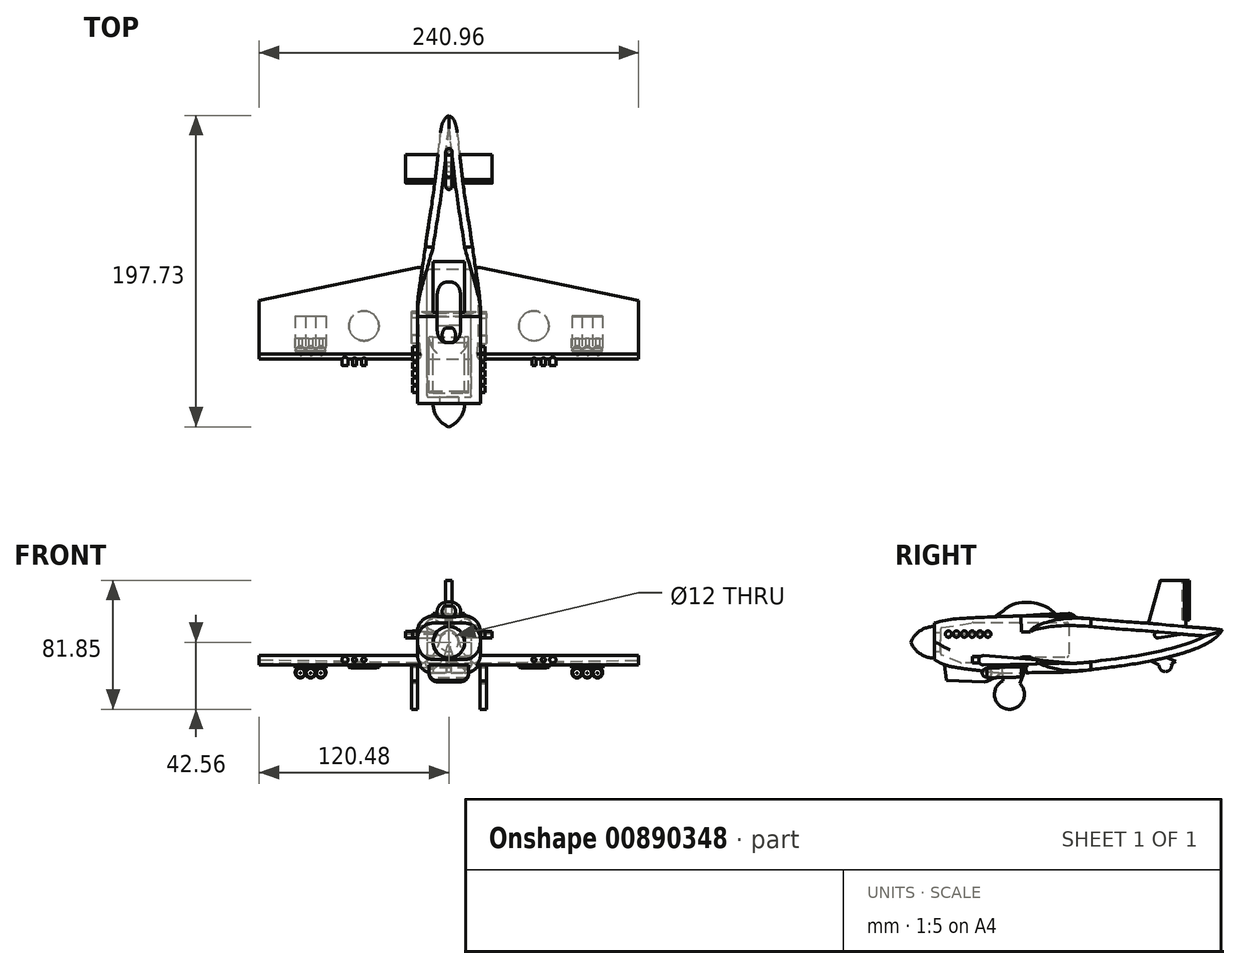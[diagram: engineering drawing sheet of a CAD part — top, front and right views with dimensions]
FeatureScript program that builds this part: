
annotation { "Feature Type Name" : "Feature", "Feature Type Description" : "" }
export const myFeature = defineFeature(function(context is Context, id is Id, definition is map)
    precondition{}
    {
        {
            var Q0;
            Q0=qCreatedBy(makeId("Right.planeOp"),FACE);
            var sketch = newSketch(context, id + "F0", { "sketchPlane" : qUnion([Q0])});
            skFitSpline(sketch, "E0", {"points": [v(0, 16.72) * mm, v(-14.24, 16.3) * mm, v(-32.71, 15.45) * mm, v(-55.08, 12.2) * mm], "startDerivative": vector(-47.41, -1.42) * mm, "endDerivative": vector(-61.1, -20.37) * mm});
            skFitSpline(sketch, "E1", {"points": [v(-55.08, -10.92) * mm, v(-48.5, -14.3) * mm, v(-31.02, -17.4) * mm, v(-12.83, -19.38) * mm, v(0, -19.52) * mm], "startDerivative": vector(34.18, -18.97) * mm, "endDerivative": vector(51.38, 0.82) * mm});
            skLineSegment(sketch, "E2", {"start": v(-55.08, 12.2) * mm, "end": v(-55.08, -10.92) * mm});
            skFitSpline(sketch, "E3", {"points": [v(0, -19.52) * mm, v(26.25, -19.04) * mm, v(50.38, -16.63) * mm, v(79.55, -12.4) * mm, v(113.94, -2.75) * mm, v(127.82, 7.9) * mm], "startDerivative": vector(117.96, 7.06) * mm, "endDerivative": vector(47.77, 80.25) * mm});
            skFitSpline(sketch, "E4", {"points": [v(0, 16.72) * mm, v(21.14, 16.46) * mm, v(44.97, 14.87) * mm, v(59.73, 13.57) * mm, v(82.02, 11.97) * mm, v(103.34, 10.02) * mm, v(127.82, 7.9) * mm], "startDerivative": vector(116.94, -1.03) * mm, "endDerivative": vector(53.67, -10.38) * mm});
            skLineSegment(sketch, "E5", {"start": v(-14.24, 16.3) * mm, "end": v(-12.51, 5.87) * mm});
            skLineSegment(sketch, "E6", {"start": v(-12.51, 5.87) * mm, "end": v(-15.87, -4.9) * mm});
            skLineSegment(sketch, "E7", {"start": v(-15.87, -4.9) * mm, "end": v(-23.28, -12.46) * mm});
            skLineSegment(sketch, "E8", {"start": v(-23.28, -12.46) * mm, "end": v(-31.02, -17.4) * mm});
            skLineSegment(sketch, "E9", {"start": v(-48.5, -14.3) * mm, "end": v(-47.42, -24.3) * mm});
            skLineSegment(sketch, "E10", {"start": v(-47.42, -24.3) * mm, "end": v(-22.16, -25.07) * mm});
            skLineSegment(sketch, "E11", {"start": v(-22.16, -25.07) * mm, "end": v(-16.61, -22.51) * mm});
            skLineSegment(sketch, "E12", {"start": v(-16.61, -22.51) * mm, "end": v(-12.83, -19.38) * mm});
            skSolve(sketch);
        }
        {
            var Q0;
            Q0=makeQuery(id+"F0.imprint","IMPRINT",FACE,{"disambiguationData":[TD([[makeQuery(id+"F0.imprint","IMPRINT",EDGE,{"derivedFrom":sQuery(id+"F0.wireOp",EDGE,"E0")}),1.0]])]});
            var Q1;
            {var subQ1=sQuery(id+"F0.wireOp",EDGE,"E3");Q1=makeQuery(id+"F0.imprint","IMPRINT",FACE,{"disambiguationData":[TD([[makeQuery(id+"F0.imprint","IMPRINT",EDGE,{"derivedFrom":subQ1}),1.0]])]});}
            extrude(context, id + "F1", {"entities" : qUnion([Q0, Q1]), "oppositeDirection" : true, "depth" : 20 * mm, "offsetDistance" : 25 * mm});
        }
        {
            var Q0;
            Q0=makeQuery(id+"F1.opExtrude","CAP_EDGE",EDGE,{"disambiguationData":[OSD([sQuery(id+"F0.wireOp",EDGE,"E4")])],"isStart":false});
            var Q1;
            Q1=makeQuery(id+"F1.opExtrude","CAP_EDGE",EDGE,{"disambiguationData":[OSD([sQuery(id+"F0.wireOp",EDGE,"E0")])],"isStart":false});
            var Q2;
            Q2=makeQuery(id+"F1.opExtrude","CAP_EDGE",EDGE,{"disambiguationData":[OSD([sQuery(id+"F0.wireOp",EDGE,"E3")])],"isStart":false});
            var Q3;
            Q3=makeQuery(id+"F1.opExtrude","CAP_EDGE",EDGE,{"disambiguationData":[OSD([sQuery(id+"F0.wireOp",EDGE,"E1")])],"isStart":false});
            fillet(context, id + "F2", {"entities" : qUnion([Q0, Q1, Q2, Q3]), "radius" : 10 * mm, "tangentPropagation" : true, "allowEdgeOverflow" : false});
        }
        {
            var Q0;
            Q0=qCreatedBy(makeId("Top.planeOp"),FACE);
            var sketch = newSketch(context, id + "F3", { "sketchPlane" : qUnion([Q0])});
            skFitSpline(sketch, "E13", {"points": [v(-3.69, 127.82) * mm, v(-8.55, 88.27) * mm, v(-13.04, 57.18) * mm, v(-17.19, 28.87) * mm, v(-20.17, 0) * mm], "startDerivative": vector(-19.1, -98.98) * mm, "endDerivative": vector(1.04, -111.2) * mm});
            skFitSpline(sketch, "E14.MirrorCS", {"points": [v(3.69, 127.82) * mm, v(8.55, 88.27) * mm, v(13.04, 57.18) * mm, v(17.19, 28.87) * mm, v(20.17, 0) * mm], "startDerivative": vector(19.1, -98.98) * mm, "endDerivative": vector(-1.04, -111.2) * mm});
            skLineSegment(sketch, "E15.bottom", {"start": v(-50.38, -63.43) * mm, "end": v(41.73, -63.43) * mm});
            skLineSegment(sketch, "E15.top", {"start": v(-50.38, 132.63) * mm, "end": v(41.73, 132.63) * mm});
            skLineSegment(sketch, "E15.left", {"start": v(-50.38, -63.43) * mm, "end": v(-50.38, 132.63) * mm});
            skLineSegment(sketch, "E15.right", {"start": v(41.73, -63.43) * mm, "end": v(41.73, 132.63) * mm});
            skLineSegment(sketch, "E16", {"start": v(-20.17, 0) * mm, "end": v(-50.38, 0) * mm});
            skLineSegment(sketch, "E17", {"start": v(20.17, 0) * mm, "end": v(41.73, 0) * mm});
            skLineSegment(sketch, "E18", {"start": v(-3.69, 127.82) * mm, "end": v(3.69, 127.82) * mm});
            skSolve(sketch);
        }
        {
            var Q0;
            Q0=makeQuery(id+"F3.imprint","IMPRINT",FACE,{"disambiguationData":[TD([[makeQuery(id+"F3.imprint","IMPRINT",EDGE,{"derivedFrom":sQuery(id+"F3.wireOp",EDGE,"E13")}),-1.0]])]});
            extrude(context, id + "F4", {"entities" : qUnion([Q0]), "operationType" : NewBodyOperationType.REMOVE, "oppositeDirection" : true, "depth" : 100 * mm, "offsetDistance" : 25 * mm, "symmetric" : true});
        }
        {
            var Q0;
            {var subQ0=sQuery(id+"F0.wireOp",EDGE,"E4");Q0=makeQuery(id+"F4.boolean.opBoolean","INTERSECT",EDGE,{"derivedFrom":[makeQuery(id+"F2.opFillet","BLEND_FACE",FACE,{"disambiguationData":[OSD([subQ0]),TDD([makeQuery(id+"F1.opExtrude","CAP_EDGE",EDGE,{"disambiguationData":[OSD([subQ0])],"isStart":true})])]}),makeQuery(id+"F4.opExtrude","SWEPT_FACE",FACE,{"disambiguationData":[OSD([sQuery(id+"F3.wireOp",EDGE,"E13")])]})]});}
            var Q1;
            {var subQ0=sQuery(id+"F0.wireOp",EDGE,"E4");Q1=makeQuery(id+"F4.boolean.opBoolean","INTERSECT",EDGE,{"derivedFrom":[makeQuery(id+"F2.opFillet","BLEND_FACE",FACE,{"disambiguationData":[OSD([subQ0]),TDD([makeQuery(id+"F1.opExtrude","CAP_EDGE",EDGE,{"disambiguationData":[OSD([subQ0])],"isStart":false})])]}),makeQuery(id+"F4.opExtrude","SWEPT_FACE",FACE,{"disambiguationData":[OSD([sQuery(id+"F3.wireOp",EDGE,"E14.MirrorCS")])]})]});}
            fillet(context, id + "F5", {"entities" : qUnion([Q0, Q1]), "radius" : 5 * mm, "tangentPropagation" : true, "allowEdgeOverflow" : false});
        }
        {
            var Q0;
            Q0=qCreatedBy(makeId("Right.planeOp"),FACE);
            var sketch = newSketch(context, id + "F6", { "sketchPlane" : qUnion([Q0])});
            skLineSegment(sketch, "E19", {"start": v(-16.45, 16.22) * mm, "end": v(-7.08, 23.21) * mm});
            skLineSegment(sketch, "E20", {"start": v(-7.08, 23.21) * mm, "end": v(-5.77, 16.56) * mm});
            skLineSegment(sketch, "E21", {"start": v(-5.77, 16.56) * mm, "end": v(-16.45, 16.22) * mm});
            skArc(sketch, "E22", {"start": v(21.96, 18.06) * mm, "mid": v(8.23, 25.06) * mm, "end": v(-7.08, 23.21) * mm});
            skLineSegment(sketch, "E23", {"start": v(-5.77, 16.56) * mm, "end": v(21.96, 18.06) * mm});
            skLineSegment(sketch, "E24", {"start": v(2.5, 16.7) * mm, "end": v(32.72, 18.34) * mm});
            skLineSegment(sketch, "E25", {"start": v(32.72, 18.34) * mm, "end": v(34.89, 15.69) * mm});
            skLineSegment(sketch, "E26", {"start": v(2.5, 16.7) * mm, "end": v(34.89, 15.69) * mm});
            skSolve(sketch);
        }
        {
            var Q0;
            Q0=makeQuery(id+"F6.imprint","IMPRINT",FACE,{"disambiguationData":[TD([[makeQuery(id+"F6.imprint","IMPRINT",EDGE,{"derivedFrom":sQuery(id+"F6.wireOp",EDGE,"E24")}),-1.0]])]});
            extrude(context, id + "F7", {"entities" : qUnion([Q0]), "operationType" : NewBodyOperationType.ADD, "oppositeDirection" : true, "depth" : 10 * mm, "offsetDistance" : 25 * mm});
        }
        {
            var Q0;
            Q0=makeQuery(id+"F6.imprint","IMPRINT",FACE,{"disambiguationData":[TD([[makeQuery(id+"F6.imprint","IMPRINT",EDGE,{"derivedFrom":sQuery(id+"F6.wireOp",EDGE,"E19")}),-1.0]])]});
            extrude(context, id + "F8", {"entities" : qUnion([Q0]), "operationType" : NewBodyOperationType.ADD, "oppositeDirection" : true, "depth" : 7.5 * mm, "offsetDistance" : 25 * mm});
        }
        {
            var Q0;
            Q0=makeQuery(id+"F6.imprint","IMPRINT",FACE,{"disambiguationData":[TD([[makeQuery(id+"F6.imprint","IMPRINT",EDGE,{"derivedFrom":sQuery(id+"F6.wireOp",EDGE,"E20")}),1.0]])]});
            extrude(context, id + "F9", {"entities" : qUnion([Q0]), "operationType" : NewBodyOperationType.ADD, "oppositeDirection" : true, "depth" : 7.5 * mm, "offsetDistance" : 25 * mm});
        }
        {
            var Q0;
            Q0=qCreatedBy(makeId("Right.planeOp"),FACE);
            var sketch = newSketch(context, id + "F10", { "sketchPlane" : qUnion([Q0])});
            skLineSegment(sketch, "E27", {"start": v(-51.08, 9.2) * mm, "end": v(-51.08, -7.92) * mm});
            skLineSegment(sketch, "E28", {"start": v(-51.08, 9.2) * mm, "end": v(-30.67, 12.45) * mm});
            skLineSegment(sketch, "E29", {"start": v(-30.67, 12.45) * mm, "end": v(-15.87, 12.45) * mm});
            skLineSegment(sketch, "E30", {"start": v(-15.87, 12.45) * mm, "end": v(-15.87, -13.07) * mm});
            skLineSegment(sketch, "E31", {"start": v(-15.87, -13.07) * mm, "end": v(-38.15, -13.07) * mm});
            skLineSegment(sketch, "E32", {"start": v(-38.15, -13.07) * mm, "end": v(-51.08, -7.92) * mm});
            skLineSegment(sketch, "E33.bottom", {"start": v(-15.87, 12.45) * mm, "end": v(30.26, 12.45) * mm});
            skLineSegment(sketch, "E33.top", {"start": v(-15.87, -9.27) * mm, "end": v(30.26, -9.27) * mm});
            skLineSegment(sketch, "E33.left", {"start": v(-15.87, 12.45) * mm, "end": v(-15.87, -9.27) * mm});
            skLineSegment(sketch, "E33.right", {"start": v(30.26, 12.45) * mm, "end": v(30.26, -9.27) * mm});
            skSolve(sketch);
        }
        {
            var Q0;
            Q0=makeQuery(id+"F10.imprint","IMPRINT",FACE,{"disambiguationData":[TD([[makeQuery(id+"F10.imprint","IMPRINT",EDGE,{"derivedFrom":sQuery(id+"F10.wireOp",EDGE,"E27")}),1.0]])]});
            var Q1;
            Q1=makeQuery(id+"F10.imprint","IMPRINT",FACE,{"disambiguationData":[TD([[makeQuery(id+"F10.imprint","IMPRINT",EDGE,{"derivedFrom":sQuery(id+"F10.wireOp",EDGE,"E33.bottom")}),-1.0]])]});
            extrude(context, id + "F11", {"entities" : qUnion([Q0, Q1]), "operationType" : NewBodyOperationType.REMOVE, "oppositeDirection" : true, "depth" : 14 * mm, "offsetDistance" : 25 * mm});
        }
        {
            var Q0;
            Q0=makeQuery(id+"F9.opExtrude","CAP_EDGE",EDGE,{"disambiguationData":[OSD([sQuery(id+"F6.wireOp",EDGE,"E22")])],"isStart":false});
            fillet(context, id + "F12", {"entities" : qUnion([Q0]), "radius" : 6 * mm, "tangentPropagation" : true, "allowEdgeOverflow" : false});
        }
        {
            var Q0;
            Q0=makeQuery(id+"F1.opExtrude","SWEPT_FACE",FACE,{"disambiguationData":[OSD([sQuery(id+"F0.wireOp",EDGE,"E2")])]});
            var sketch = newSketch(context, id + "F13", { "sketchPlane" : qUnion([Q0])});
            skCircle(sketch, "E34", {"center": v(0, 0) * mm, "radius": 6 * mm});
            skSolve(sketch);
        }
        {
            var Q0;
            {var subQ0=sQuery(id+"F13.wireOp",EDGE,"E34");var subQ1=makeQuery(id+"F1.opExtrude","CAP_EDGE",EDGE,{"disambiguationData":[OSD([sQuery(id+"F0.wireOp",EDGE,"E2")])],"isStart":true});var subQ2=makeQuery(id+"F13.imprint","INTERSECT",VERTEX,{"disambiguationData":[OD(0.0)],"derivedFrom":[subQ1,subQ0]});Q0=makeQuery(id+"F13.imprint","IMPRINT",FACE,{"disambiguationData":[TD([[makeQuery(id+"F13.imprint","IMPRINT",EDGE,{"disambiguationData":[TD([[subQ2,-1.0]])],"derivedFrom":subQ0}),1.0]])]});}
            extrude(context, id + "F14", {"entities" : qUnion([Q0]), "operationType" : NewBodyOperationType.REMOVE, "oppositeDirection" : true, "depth" : 25 * mm, "offsetDistance" : 25 * mm});
        }
        {
            var Q0;
            Q0=qCreatedBy(makeId("Right.planeOp"),FACE);
            var sketch = newSketch(context, id + "F15", { "sketchPlane" : qUnion([Q0])});
            skArc(sketch, "E35", {"start": v(-23.86, -8.47) * mm, "mid": v(-26.86, -11.47) * mm, "end": v(-23.86, -14.47) * mm});
            skLineSegment(sketch, "E36", {"start": v(-23.86, -8.47) * mm, "end": v(31.14, -13.1) * mm});
            skLineSegment(sketch, "E37", {"start": v(31.14, -13.1) * mm, "end": v(-23.86, -14.47) * mm});
            skArc(sketch, "E38", {"start": v(87.08, 6.72) * mm, "mid": v(84.75, 4.75) * mm, "end": v(87.08, 2.78) * mm});
            skLineSegment(sketch, "E39", {"start": v(87.08, 6.72) * mm, "end": v(103.03, 5.17) * mm});
            skLineSegment(sketch, "E40", {"start": v(103.03, 5.17) * mm, "end": v(87.08, 2.78) * mm});
            skSolve(sketch);
        }
        {
            var Q0;
            Q0=makeQuery(id+"F15.imprint","IMPRINT",FACE,{"disambiguationData":[TD([[makeQuery(id+"F15.imprint","IMPRINT",EDGE,{"derivedFrom":sQuery(id+"F15.wireOp",EDGE,"E35")}),1.0]])]});
            extrude(context, id + "F16", {"entities" : qUnion([Q0]), "operationType" : NewBodyOperationType.ADD, "oppositeDirection" : true, "depth" : 25 * mm, "offsetDistance" : 25 * mm});
        }
        {
            var Q0;
            Q0=makeQuery(id+"F16.opExtrude","CAP_FACE",FACE,{"disambiguationData":[OSD([sQuery(id+"F15.wireOp",EDGE,"E35"),sQuery(id+"F15.wireOp",EDGE,"E36"),sQuery(id+"F15.wireOp",EDGE,"E37")])],"isStart":false});
            extrude(context, id + "F17", {"entities" : qUnion([Q0]), "operationType" : NewBodyOperationType.ADD, "depth" : 100 * mm, "offsetDistance" : 25 * mm});
        }
        {
            var Q0;
            {var subQ0=sQuery(id+"F15.wireOp",EDGE,"E36");var subQ4=sQuery(id+"F0.wireOp",EDGE,"E1");Q0=makeQuery(id+"F17.boolean.opBoolean","MERGE",FACE,{"derivedFrom":[makeQuery(id+"F16.boolean.opBoolean","SPLIT",FACE,{"disambiguationData":[TD([makeQuery(id+"F2.opFillet","BLEND_FACE",FACE,{"disambiguationData":[OSD([subQ4]),TDD([makeQuery(id+"F1.opExtrude","CAP_EDGE",EDGE,{"disambiguationData":[OSD([subQ4])],"isStart":false})])]})])],"derivedFrom":makeQuery(id+"F16.opExtrude","SWEPT_FACE",FACE,{"disambiguationData":[OSD([subQ0])]})}),makeQuery(id+"F17.opExtrude","SWEPT_FACE",FACE,{"disambiguationData":[OSD([subQ0])]})]});}
            var sketch = newSketch(context, id + "F18", { "sketchPlane" : qUnion([Q0])});
            skLineSegment(sketch, "E41", {"start": v(19.74, 32.12) * mm, "end": v(120.48, 11.31) * mm});
            skLineSegment(sketch, "E42", {"start": v(120.48, 11.31) * mm, "end": v(120.48, -23.07) * mm});
            skLineSegment(sketch, "E43", {"start": v(120.48, -23.07) * mm, "end": v(-125, -23.07) * mm});
            skLineSegment(sketch, "E44", {"start": v(19.74, 32.12) * mm, "end": v(22.37, 44.82) * mm});
            skLineSegment(sketch, "E45", {"start": v(22.37, 44.82) * mm, "end": v(134.96, 44.82) * mm});
            skLineSegment(sketch, "E46", {"start": v(134.96, 44.82) * mm, "end": v(134.96, -23.07) * mm});
            skLineSegment(sketch, "E47", {"start": v(134.96, -23.07) * mm, "end": v(120.48, -23.07) * mm});
            skLineSegment(sketch, "E48", {"start": v(120.48, -23.07) * mm, "end": v(120.48, -30.04) * mm});
            skLineSegment(sketch, "E49", {"start": v(120.48, -30.04) * mm, "end": v(134.77, -30) * mm});
            skLineSegment(sketch, "E50", {"start": v(134.77, -30) * mm, "end": v(134.96, -23.07) * mm});
            skLineSegment(sketch, "E51.MirrorCS", {"start": v(-22.37, 44.82) * mm, "end": v(-134.96, 44.82) * mm});
            skLineSegment(sketch, "E52.MirrorCS", {"start": v(-19.74, 32.12) * mm, "end": v(-22.37, 44.82) * mm});
            skLineSegment(sketch, "E53.MirrorCS", {"start": v(-19.74, 32.12) * mm, "end": v(-120.48, 11.31) * mm});
            skLineSegment(sketch, "E54.MirrorCS", {"start": v(-134.96, 44.82) * mm, "end": v(-134.96, -23.07) * mm});
            skLineSegment(sketch, "E55.MirrorCS", {"start": v(-120.48, -30.04) * mm, "end": v(-134.77, -30) * mm});
            skLineSegment(sketch, "E56.MirrorCS", {"start": v(-120.48, -23.07) * mm, "end": v(-120.48, -30.04) * mm});
            skLineSegment(sketch, "E57.MirrorCS", {"start": v(-134.77, -30) * mm, "end": v(-134.96, -23.07) * mm});
            skLineSegment(sketch, "E58.MirrorCS", {"start": v(-120.48, 11.31) * mm, "end": v(-120.48, -23.07) * mm});
            skSolve(sketch);
        }
        {
            var Q0;
            Q0=makeQuery(id+"F18.imprint","IMPRINT",FACE,{"disambiguationData":[TD([[makeQuery(id+"F18.imprint","IMPRINT",EDGE,{"derivedFrom":sQuery(id+"F18.wireOp",EDGE,"E51.MirrorCS")}),1.0]])]});
            var Q1;
            {var subQ1=sQuery(id+"F18.wireOp",EDGE,"E53.MirrorCS");Q1=makeQuery(id+"F18.imprint","IMPRINT",FACE,{"disambiguationData":[TD([[makeQuery(id+"F18.imprint","IMPRINT",EDGE,{"derivedFrom":subQ1}),-1.0]])]});}
            extrude(context, id + "F19", {"entities" : qUnion([Q0, Q1]), "operationType" : NewBodyOperationType.REMOVE, "oppositeDirection" : true, "depth" : 25 * mm, "offsetDistance" : 25 * mm});
        }
        {
            var Q0;
            Q0=qCreatedBy(makeId("Right.planeOp"),FACE);
            var sketch = newSketch(context, id + "F20", { "sketchPlane" : qUnion([Q0])});
            skLineSegment(sketch, "E59", {"start": v(80.82, 12.07) * mm, "end": v(88.57, 39.3) * mm});
            skLineSegment(sketch, "E60", {"start": v(88.57, 39.3) * mm, "end": v(104.75, 39.3) * mm});
            skLineSegment(sketch, "E61", {"start": v(104.75, 39.3) * mm, "end": v(104.75, 9.9) * mm});
            skLineSegment(sketch, "E62", {"start": v(104.75, 9.9) * mm, "end": v(80.82, 12.07) * mm});
            skLineSegment(sketch, "E63.bottom", {"start": v(106.73, 39.3) * mm, "end": v(118.95, 39.3) * mm});
            skLineSegment(sketch, "E63.top", {"start": v(106.73, 11.19) * mm, "end": v(118.95, 11.19) * mm});
            skLineSegment(sketch, "E63.left", {"start": v(106.73, 39.3) * mm, "end": v(106.73, 11.19) * mm});
            skLineSegment(sketch, "E63.right", {"start": v(118.95, 39.3) * mm, "end": v(118.95, 11.19) * mm});
            skLineSegment(sketch, "E64.bottom", {"start": v(104.75, 34.79) * mm, "end": v(106.73, 34.79) * mm});
            skLineSegment(sketch, "E64.top", {"start": v(104.75, 31.59) * mm, "end": v(106.73, 31.59) * mm});
            skLineSegment(sketch, "E64.left", {"start": v(104.75, 34.79) * mm, "end": v(104.75, 31.59) * mm});
            skLineSegment(sketch, "E64.right", {"start": v(106.73, 34.79) * mm, "end": v(106.73, 31.59) * mm});
            skLineSegment(sketch, "E65.bottom", {"start": v(104.75, 22.93) * mm, "end": v(106.73, 22.93) * mm});
            skLineSegment(sketch, "E65.top", {"start": v(104.75, 18.78) * mm, "end": v(106.73, 18.78) * mm});
            skLineSegment(sketch, "E65.left", {"start": v(104.75, 22.93) * mm, "end": v(104.75, 18.78) * mm});
            skLineSegment(sketch, "E65.right", {"start": v(106.73, 22.93) * mm, "end": v(106.73, 18.78) * mm});
            skLineSegment(sketch, "E66", {"start": v(80.82, 12.07) * mm, "end": v(80.49, 8.43) * mm});
            skLineSegment(sketch, "E67", {"start": v(80.49, 8.43) * mm, "end": v(104.27, 6.28) * mm});
            skLineSegment(sketch, "E68", {"start": v(104.27, 6.28) * mm, "end": v(104.75, 9.9) * mm});
            skSolve(sketch);
        }
        {
            var Q0;
            Q0=makeQuery(id+"F20.imprint","IMPRINT",FACE,{"disambiguationData":[TD([[makeQuery(id+"F20.imprint","IMPRINT",EDGE,{"derivedFrom":sQuery(id+"F20.wireOp",EDGE,"E59")}),-1.0]])]});
            var Q1;
            Q1=makeQuery(id+"F20.imprint","IMPRINT",FACE,{"disambiguationData":[TD([[makeQuery(id+"F20.imprint","IMPRINT",EDGE,{"derivedFrom":sQuery(id+"F20.wireOp",EDGE,"E62")}),1.0]])]});
            extrude(context, id + "F21", {"entities" : qUnion([Q0, Q1]), "operationType" : NewBodyOperationType.ADD, "oppositeDirection" : true, "depth" : 2 * mm, "offsetDistance" : 25 * mm});
        }
        {
            var Q0;
            Q0=makeQuery(id+"F21.opExtrude","SWEPT_FACE",FACE,{"disambiguationData":[OSD([sQuery(id+"F20.wireOp",EDGE,"E60")])]});
            var sketch = newSketch(context, id + "F22", { "sketchPlane" : qUnion([Q0])});
            skArc(sketch, "E69", {"start": v(0, 102.75) * mm, "mid": v(-2, 104.75) * mm, "end": v(0, 106.75) * mm});
            skArc(sketch, "E70", {"start": v(0, 102.55) * mm, "mid": v(-1.56, 103.19) * mm, "end": v(-2.2, 104.75) * mm});
            skLineSegment(sketch, "E71", {"start": v(-2, 104.75) * mm, "end": v(0, 119.75) * mm});
            skLineSegment(sketch, "E72", {"start": v(0, 119.75) * mm, "end": v(0, 104.75) * mm});
            skLineSegment(sketch, "E73", {"start": v(0, 102.55) * mm, "end": v(0, 102.75) * mm});
            skLineSegment(sketch, "E74", {"start": v(0, 102.75) * mm, "end": v(0, 104.75) * mm});
            skLineSegment(sketch, "E75", {"start": v(0, 104.75) * mm, "end": v(-2, 104.75) * mm});
            skSolve(sketch);
        }
        {
            var Q0;
            {var subQ2=sQuery(id+"F22.wireOp",EDGE,"E74");Q0=makeQuery(id+"F22.imprint","IMPRINT",FACE,{"disambiguationData":[TD([[makeQuery(id+"F22.imprint","IMPRINT",EDGE,{"derivedFrom":subQ2}),1.0]])]});}
            var Q1;
            {var subQ5=sQuery(id+"F22.wireOp",EDGE,"E75");Q1=makeQuery(id+"F22.imprint","IMPRINT",FACE,{"disambiguationData":[TD([[makeQuery(id+"F22.imprint","IMPRINT",EDGE,{"derivedFrom":subQ5}),1.0]])]});}
            var Q2;
            {var subQ0=sQuery(id+"F22.wireOp",EDGE,"E72");var subQ1=sQuery(id+"F22.wireOp",EDGE,"E69");var subQ2=makeQuery(id+"F22.imprint","INTERSECT",VERTEX,{"derivedFrom":[subQ1,subQ0]});Q2=makeQuery(id+"F22.imprint","IMPRINT",FACE,{"disambiguationData":[TD([[makeQuery(id+"F22.imprint","IMPRINT",EDGE,{"disambiguationData":[TD([[subQ2,1.0]])],"derivedFrom":subQ1}),1.0]])]});}
            extrude(context, id + "F23", {"entities" : qUnion([Q0, Q1, Q2]), "operationType" : NewBodyOperationType.ADD, "oppositeDirection" : true, "depth" : 25 * mm, "offsetDistance" : 25 * mm});
        }
        {
            var Q0;
            {var subQ4=sQuery(id+"F22.wireOp",EDGE,"E73");Q0=makeQuery(id+"F22.imprint","IMPRINT",FACE,{"disambiguationData":[TD([[makeQuery(id+"F22.imprint","IMPRINT",EDGE,{"derivedFrom":subQ4}),1.0]])]});}
            extrude(context, id + "F24", {"entities" : qUnion([Q0]), "operationType" : NewBodyOperationType.REMOVE, "oppositeDirection" : true, "depth" : 25 * mm, "offsetDistance" : 25 * mm});
        }
        {
            var Q0;
            Q0=makeQuery(id+"F1.opExtrude","SWEPT_FACE",FACE,{"disambiguationData":[OSD([sQuery(id+"F0.wireOp",EDGE,"E2")])]});
            var sketch = newSketch(context, id + "F25", { "sketchPlane" : qUnion([Q0])});
            skCircle(sketch, "E76", {"center": v(0, 0) * mm, "radius": 10 * mm});
            skSolve(sketch);
        }
        {
            var Q0;
            Q0=qCreatedBy(makeId("Right.planeOp"),FACE);
            var sketch = newSketch(context, id + "F26", { "sketchPlane" : qUnion([Q0])});
            skArc(sketch, "E77", {"start": v(-55.08, 10) * mm, "mid": v(-64.1, 7.3) * mm, "end": v(-70.03, 0) * mm});
            skArc(sketch, "E78.MirrorCS", {"start": v(-55.08, -10) * mm, "mid": v(-64.1, -7.3) * mm, "end": v(-70.03, 0) * mm});
            skLineSegment(sketch, "E79", {"start": v(-70.03, 0) * mm, "end": v(-55.08, 0) * mm});
            skLineSegment(sketch, "E80", {"start": v(-55.08, 10) * mm, "end": v(-55.08, -10) * mm});
            skSolve(sketch);
        }
        {
            var Q0;
            {var subQ0=sQuery(id+"F26.wireOp",EDGE,"E77");Q0=makeQuery(id+"F26.imprint","IMPRINT",FACE,{"disambiguationData":[TD([[makeQuery(id+"F26.imprint","IMPRINT",EDGE,{"derivedFrom":subQ0}),1.0]])]});}
            var Q1;
            Q1=sQuery(id+"F26.wireOp",EDGE,"E79");
            revolve(context, id + "F27", {"surfaceOperationType" : NewSurfaceOperationType.NEW, "entities" : qUnion([Q0]), "axis" : qUnion([Q1]), "revolveType" : RevolveType.FULL});
        }
        {
            var Q0;
            Q0=makeQuery(id+"F1.opExtrude","CAP_FACE",FACE,{"disambiguationData":[OSD([sQuery(id+"F0.wireOp",EDGE,"E0"),sQuery(id+"F0.wireOp",EDGE,"E1"),sQuery(id+"F0.wireOp",EDGE,"E2"),sQuery(id+"F0.wireOp",EDGE,"E3"),sQuery(id+"F0.wireOp",EDGE,"E4")])],"isStart":false});
            var sketch = newSketch(context, id + "F28", { "sketchPlane" : qUnion([Q0])});
            skCircle(sketch, "E81", {"center": v(26.08, 5.2) * mm, "radius": 2 * mm});
            skCircle(sketch, "E82", {"center": v(31.08, 5.2) * mm, "radius": 2 * mm});
            skCircle(sketch, "E83", {"center": v(36.08, 5.2) * mm, "radius": 2 * mm});
            skCircle(sketch, "E84", {"center": v(41.08, 5.2) * mm, "radius": 2 * mm});
            skCircle(sketch, "E85", {"center": v(46.08, 5.2) * mm, "radius": 2 * mm});
            skCircle(sketch, "E86", {"center": v(21.08, 5.2) * mm, "radius": 2 * mm});
            skSolve(sketch);
        }
        {
            var Q0;
            {var subQ0=sQuery(id+"F28.wireOp",EDGE,"E86");var subQ1=sQuery(id+"F0.wireOp",EDGE,"E0");var subQ2=makeQuery(id+"F2.opFillet","BLEND_EDGE",EDGE,{"blendedFrom":[makeQuery(id+"F1.opExtrude","CAP_EDGE",EDGE,{"disambiguationData":[OSD([subQ1])],"isStart":false}),makeQuery(id+"F1.opExtrude","CAP_FACE",FACE,{"disambiguationData":[OSD([subQ1,sQuery(id+"F0.wireOp",EDGE,"E1"),sQuery(id+"F0.wireOp",EDGE,"E2"),sQuery(id+"F0.wireOp",EDGE,"E3"),sQuery(id+"F0.wireOp",EDGE,"E4")])],"isStart":false})],"blendedInto":[makeQuery(id+"F1.opExtrude","CAP_FACE",FACE,{"disambiguationData":[OSD([subQ1,sQuery(id+"F0.wireOp",EDGE,"E1"),sQuery(id+"F0.wireOp",EDGE,"E2"),sQuery(id+"F0.wireOp",EDGE,"E3"),sQuery(id+"F0.wireOp",EDGE,"E4")])],"isStart":false})]});var subQ3=makeQuery(id+"F28.imprint","INTERSECT",VERTEX,{"disambiguationData":[OD(0.0)],"derivedFrom":[subQ2,subQ0]});Q0=makeQuery(id+"F28.imprint","IMPRINT",FACE,{"disambiguationData":[TD([[makeQuery(id+"F28.imprint","IMPRINT",EDGE,{"disambiguationData":[TD([[subQ3,1.0]])],"derivedFrom":subQ0}),1.0]])]});}
            var Q1;
            {var subQ0=sQuery(id+"F28.wireOp",EDGE,"E86");var subQ1=sQuery(id+"F0.wireOp",EDGE,"E0");var subQ2=makeQuery(id+"F2.opFillet","BLEND_EDGE",EDGE,{"blendedFrom":[makeQuery(id+"F1.opExtrude","CAP_EDGE",EDGE,{"disambiguationData":[OSD([subQ1])],"isStart":false}),makeQuery(id+"F1.opExtrude","CAP_FACE",FACE,{"disambiguationData":[OSD([subQ1,sQuery(id+"F0.wireOp",EDGE,"E1"),sQuery(id+"F0.wireOp",EDGE,"E2"),sQuery(id+"F0.wireOp",EDGE,"E3"),sQuery(id+"F0.wireOp",EDGE,"E4")])],"isStart":false})],"blendedInto":[makeQuery(id+"F1.opExtrude","CAP_FACE",FACE,{"disambiguationData":[OSD([subQ1,sQuery(id+"F0.wireOp",EDGE,"E1"),sQuery(id+"F0.wireOp",EDGE,"E2"),sQuery(id+"F0.wireOp",EDGE,"E3"),sQuery(id+"F0.wireOp",EDGE,"E4")])],"isStart":false})]});var subQ3=makeQuery(id+"F28.imprint","INTERSECT",VERTEX,{"disambiguationData":[OD(0.0)],"derivedFrom":[subQ2,subQ0]});Q1=makeQuery(id+"F28.imprint","IMPRINT",FACE,{"disambiguationData":[TD([[makeQuery(id+"F28.imprint","IMPRINT",EDGE,{"disambiguationData":[TD([[subQ3,-1.0]])],"derivedFrom":subQ0}),1.0]])]});}
            var Q2;
            {var subQ0=sQuery(id+"F28.wireOp",EDGE,"E81");var subQ1=sQuery(id+"F0.wireOp",EDGE,"E0");var subQ2=makeQuery(id+"F2.opFillet","BLEND_EDGE",EDGE,{"blendedFrom":[makeQuery(id+"F1.opExtrude","CAP_EDGE",EDGE,{"disambiguationData":[OSD([subQ1])],"isStart":false}),makeQuery(id+"F1.opExtrude","CAP_FACE",FACE,{"disambiguationData":[OSD([subQ1,sQuery(id+"F0.wireOp",EDGE,"E1"),sQuery(id+"F0.wireOp",EDGE,"E2"),sQuery(id+"F0.wireOp",EDGE,"E3"),sQuery(id+"F0.wireOp",EDGE,"E4")])],"isStart":false})],"blendedInto":[makeQuery(id+"F1.opExtrude","CAP_FACE",FACE,{"disambiguationData":[OSD([subQ1,sQuery(id+"F0.wireOp",EDGE,"E1"),sQuery(id+"F0.wireOp",EDGE,"E2"),sQuery(id+"F0.wireOp",EDGE,"E3"),sQuery(id+"F0.wireOp",EDGE,"E4")])],"isStart":false})]});var subQ3=makeQuery(id+"F28.imprint","INTERSECT",VERTEX,{"disambiguationData":[OD(0.0)],"derivedFrom":[subQ2,subQ0]});Q2=makeQuery(id+"F28.imprint","IMPRINT",FACE,{"disambiguationData":[TD([[makeQuery(id+"F28.imprint","IMPRINT",EDGE,{"disambiguationData":[TD([[subQ3,-1.0]])],"derivedFrom":subQ0}),1.0]])]});}
            var Q3;
            {var subQ0=sQuery(id+"F28.wireOp",EDGE,"E81");var subQ1=sQuery(id+"F0.wireOp",EDGE,"E0");var subQ2=makeQuery(id+"F2.opFillet","BLEND_EDGE",EDGE,{"blendedFrom":[makeQuery(id+"F1.opExtrude","CAP_EDGE",EDGE,{"disambiguationData":[OSD([subQ1])],"isStart":false}),makeQuery(id+"F1.opExtrude","CAP_FACE",FACE,{"disambiguationData":[OSD([subQ1,sQuery(id+"F0.wireOp",EDGE,"E1"),sQuery(id+"F0.wireOp",EDGE,"E2"),sQuery(id+"F0.wireOp",EDGE,"E3"),sQuery(id+"F0.wireOp",EDGE,"E4")])],"isStart":false})],"blendedInto":[makeQuery(id+"F1.opExtrude","CAP_FACE",FACE,{"disambiguationData":[OSD([subQ1,sQuery(id+"F0.wireOp",EDGE,"E1"),sQuery(id+"F0.wireOp",EDGE,"E2"),sQuery(id+"F0.wireOp",EDGE,"E3"),sQuery(id+"F0.wireOp",EDGE,"E4")])],"isStart":false})]});var subQ3=makeQuery(id+"F28.imprint","INTERSECT",VERTEX,{"disambiguationData":[OD(0.0)],"derivedFrom":[subQ2,subQ0]});Q3=makeQuery(id+"F28.imprint","IMPRINT",FACE,{"disambiguationData":[TD([[makeQuery(id+"F28.imprint","IMPRINT",EDGE,{"disambiguationData":[TD([[subQ3,1.0]])],"derivedFrom":subQ0}),1.0]])]});}
            var Q4;
            {var subQ0=sQuery(id+"F28.wireOp",EDGE,"E82");var subQ1=sQuery(id+"F0.wireOp",EDGE,"E0");var subQ2=makeQuery(id+"F2.opFillet","BLEND_EDGE",EDGE,{"blendedFrom":[makeQuery(id+"F1.opExtrude","CAP_EDGE",EDGE,{"disambiguationData":[OSD([subQ1])],"isStart":false}),makeQuery(id+"F1.opExtrude","CAP_FACE",FACE,{"disambiguationData":[OSD([subQ1,sQuery(id+"F0.wireOp",EDGE,"E1"),sQuery(id+"F0.wireOp",EDGE,"E2"),sQuery(id+"F0.wireOp",EDGE,"E3"),sQuery(id+"F0.wireOp",EDGE,"E4")])],"isStart":false})],"blendedInto":[makeQuery(id+"F1.opExtrude","CAP_FACE",FACE,{"disambiguationData":[OSD([subQ1,sQuery(id+"F0.wireOp",EDGE,"E1"),sQuery(id+"F0.wireOp",EDGE,"E2"),sQuery(id+"F0.wireOp",EDGE,"E3"),sQuery(id+"F0.wireOp",EDGE,"E4")])],"isStart":false})]});var subQ3=makeQuery(id+"F28.imprint","INTERSECT",VERTEX,{"disambiguationData":[OD(0.0)],"derivedFrom":[subQ2,subQ0]});Q4=makeQuery(id+"F28.imprint","IMPRINT",FACE,{"disambiguationData":[TD([[makeQuery(id+"F28.imprint","IMPRINT",EDGE,{"disambiguationData":[TD([[subQ3,-1.0]])],"derivedFrom":subQ0}),1.0]])]});}
            var Q5;
            {var subQ0=sQuery(id+"F28.wireOp",EDGE,"E83");var subQ1=sQuery(id+"F0.wireOp",EDGE,"E0");var subQ2=makeQuery(id+"F2.opFillet","BLEND_EDGE",EDGE,{"blendedFrom":[makeQuery(id+"F1.opExtrude","CAP_EDGE",EDGE,{"disambiguationData":[OSD([subQ1])],"isStart":false}),makeQuery(id+"F1.opExtrude","CAP_FACE",FACE,{"disambiguationData":[OSD([subQ1,sQuery(id+"F0.wireOp",EDGE,"E1"),sQuery(id+"F0.wireOp",EDGE,"E2"),sQuery(id+"F0.wireOp",EDGE,"E3"),sQuery(id+"F0.wireOp",EDGE,"E4")])],"isStart":false})],"blendedInto":[makeQuery(id+"F1.opExtrude","CAP_FACE",FACE,{"disambiguationData":[OSD([subQ1,sQuery(id+"F0.wireOp",EDGE,"E1"),sQuery(id+"F0.wireOp",EDGE,"E2"),sQuery(id+"F0.wireOp",EDGE,"E3"),sQuery(id+"F0.wireOp",EDGE,"E4")])],"isStart":false})]});var subQ3=makeQuery(id+"F28.imprint","INTERSECT",VERTEX,{"disambiguationData":[OD(0.0)],"derivedFrom":[subQ2,subQ0]});Q5=makeQuery(id+"F28.imprint","IMPRINT",FACE,{"disambiguationData":[TD([[makeQuery(id+"F28.imprint","IMPRINT",EDGE,{"disambiguationData":[TD([[subQ3,1.0]])],"derivedFrom":subQ0}),1.0]])]});}
            var Q6;
            {var subQ0=sQuery(id+"F28.wireOp",EDGE,"E84");var subQ1=sQuery(id+"F0.wireOp",EDGE,"E0");var subQ2=makeQuery(id+"F2.opFillet","BLEND_EDGE",EDGE,{"blendedFrom":[makeQuery(id+"F1.opExtrude","CAP_EDGE",EDGE,{"disambiguationData":[OSD([subQ1])],"isStart":false}),makeQuery(id+"F1.opExtrude","CAP_FACE",FACE,{"disambiguationData":[OSD([subQ1,sQuery(id+"F0.wireOp",EDGE,"E1"),sQuery(id+"F0.wireOp",EDGE,"E2"),sQuery(id+"F0.wireOp",EDGE,"E3"),sQuery(id+"F0.wireOp",EDGE,"E4")])],"isStart":false})],"blendedInto":[makeQuery(id+"F1.opExtrude","CAP_FACE",FACE,{"disambiguationData":[OSD([subQ1,sQuery(id+"F0.wireOp",EDGE,"E1"),sQuery(id+"F0.wireOp",EDGE,"E2"),sQuery(id+"F0.wireOp",EDGE,"E3"),sQuery(id+"F0.wireOp",EDGE,"E4")])],"isStart":false})]});var subQ3=makeQuery(id+"F28.imprint","INTERSECT",VERTEX,{"disambiguationData":[OD(0.0)],"derivedFrom":[subQ2,subQ0]});Q6=makeQuery(id+"F28.imprint","IMPRINT",FACE,{"disambiguationData":[TD([[makeQuery(id+"F28.imprint","IMPRINT",EDGE,{"disambiguationData":[TD([[subQ3,1.0]])],"derivedFrom":subQ0}),1.0]])]});}
            var Q7;
            {var subQ0=sQuery(id+"F28.wireOp",EDGE,"E85");var subQ1=sQuery(id+"F0.wireOp",EDGE,"E0");var subQ2=makeQuery(id+"F2.opFillet","BLEND_EDGE",EDGE,{"blendedFrom":[makeQuery(id+"F1.opExtrude","CAP_EDGE",EDGE,{"disambiguationData":[OSD([subQ1])],"isStart":false}),makeQuery(id+"F1.opExtrude","CAP_FACE",FACE,{"disambiguationData":[OSD([subQ1,sQuery(id+"F0.wireOp",EDGE,"E1"),sQuery(id+"F0.wireOp",EDGE,"E2"),sQuery(id+"F0.wireOp",EDGE,"E3"),sQuery(id+"F0.wireOp",EDGE,"E4")])],"isStart":false})],"blendedInto":[makeQuery(id+"F1.opExtrude","CAP_FACE",FACE,{"disambiguationData":[OSD([subQ1,sQuery(id+"F0.wireOp",EDGE,"E1"),sQuery(id+"F0.wireOp",EDGE,"E2"),sQuery(id+"F0.wireOp",EDGE,"E3"),sQuery(id+"F0.wireOp",EDGE,"E4")])],"isStart":false})]});var subQ3=makeQuery(id+"F28.imprint","INTERSECT",VERTEX,{"disambiguationData":[OD(0.0)],"derivedFrom":[subQ2,subQ0]});Q7=makeQuery(id+"F28.imprint","IMPRINT",FACE,{"disambiguationData":[TD([[makeQuery(id+"F28.imprint","IMPRINT",EDGE,{"disambiguationData":[TD([[subQ3,1.0]])],"derivedFrom":subQ0}),1.0]])]});}
            var Q8;
            {var subQ0=sQuery(id+"F28.wireOp",EDGE,"E85");var subQ1=sQuery(id+"F0.wireOp",EDGE,"E0");var subQ2=makeQuery(id+"F2.opFillet","BLEND_EDGE",EDGE,{"blendedFrom":[makeQuery(id+"F1.opExtrude","CAP_EDGE",EDGE,{"disambiguationData":[OSD([subQ1])],"isStart":false}),makeQuery(id+"F1.opExtrude","CAP_FACE",FACE,{"disambiguationData":[OSD([subQ1,sQuery(id+"F0.wireOp",EDGE,"E1"),sQuery(id+"F0.wireOp",EDGE,"E2"),sQuery(id+"F0.wireOp",EDGE,"E3"),sQuery(id+"F0.wireOp",EDGE,"E4")])],"isStart":false})],"blendedInto":[makeQuery(id+"F1.opExtrude","CAP_FACE",FACE,{"disambiguationData":[OSD([subQ1,sQuery(id+"F0.wireOp",EDGE,"E1"),sQuery(id+"F0.wireOp",EDGE,"E2"),sQuery(id+"F0.wireOp",EDGE,"E3"),sQuery(id+"F0.wireOp",EDGE,"E4")])],"isStart":false})]});var subQ3=makeQuery(id+"F28.imprint","INTERSECT",VERTEX,{"disambiguationData":[OD(0.0)],"derivedFrom":[subQ2,subQ0]});Q8=makeQuery(id+"F28.imprint","IMPRINT",FACE,{"disambiguationData":[TD([[makeQuery(id+"F28.imprint","IMPRINT",EDGE,{"disambiguationData":[TD([[subQ3,-1.0]])],"derivedFrom":subQ0}),1.0]])]});}
            var Q9;
            {var subQ0=sQuery(id+"F28.wireOp",EDGE,"E84");var subQ1=sQuery(id+"F0.wireOp",EDGE,"E0");var subQ2=makeQuery(id+"F2.opFillet","BLEND_EDGE",EDGE,{"blendedFrom":[makeQuery(id+"F1.opExtrude","CAP_EDGE",EDGE,{"disambiguationData":[OSD([subQ1])],"isStart":false}),makeQuery(id+"F1.opExtrude","CAP_FACE",FACE,{"disambiguationData":[OSD([subQ1,sQuery(id+"F0.wireOp",EDGE,"E1"),sQuery(id+"F0.wireOp",EDGE,"E2"),sQuery(id+"F0.wireOp",EDGE,"E3"),sQuery(id+"F0.wireOp",EDGE,"E4")])],"isStart":false})],"blendedInto":[makeQuery(id+"F1.opExtrude","CAP_FACE",FACE,{"disambiguationData":[OSD([subQ1,sQuery(id+"F0.wireOp",EDGE,"E1"),sQuery(id+"F0.wireOp",EDGE,"E2"),sQuery(id+"F0.wireOp",EDGE,"E3"),sQuery(id+"F0.wireOp",EDGE,"E4")])],"isStart":false})]});var subQ3=makeQuery(id+"F28.imprint","INTERSECT",VERTEX,{"disambiguationData":[OD(0.0)],"derivedFrom":[subQ2,subQ0]});Q9=makeQuery(id+"F28.imprint","IMPRINT",FACE,{"disambiguationData":[TD([[makeQuery(id+"F28.imprint","IMPRINT",EDGE,{"disambiguationData":[TD([[subQ3,-1.0]])],"derivedFrom":subQ0}),1.0]])]});}
            var Q10;
            {var subQ0=sQuery(id+"F28.wireOp",EDGE,"E83");var subQ1=sQuery(id+"F0.wireOp",EDGE,"E0");var subQ2=makeQuery(id+"F2.opFillet","BLEND_EDGE",EDGE,{"blendedFrom":[makeQuery(id+"F1.opExtrude","CAP_EDGE",EDGE,{"disambiguationData":[OSD([subQ1])],"isStart":false}),makeQuery(id+"F1.opExtrude","CAP_FACE",FACE,{"disambiguationData":[OSD([subQ1,sQuery(id+"F0.wireOp",EDGE,"E1"),sQuery(id+"F0.wireOp",EDGE,"E2"),sQuery(id+"F0.wireOp",EDGE,"E3"),sQuery(id+"F0.wireOp",EDGE,"E4")])],"isStart":false})],"blendedInto":[makeQuery(id+"F1.opExtrude","CAP_FACE",FACE,{"disambiguationData":[OSD([subQ1,sQuery(id+"F0.wireOp",EDGE,"E1"),sQuery(id+"F0.wireOp",EDGE,"E2"),sQuery(id+"F0.wireOp",EDGE,"E3"),sQuery(id+"F0.wireOp",EDGE,"E4")])],"isStart":false})]});var subQ3=makeQuery(id+"F28.imprint","INTERSECT",VERTEX,{"disambiguationData":[OD(0.0)],"derivedFrom":[subQ2,subQ0]});Q10=makeQuery(id+"F28.imprint","IMPRINT",FACE,{"disambiguationData":[TD([[makeQuery(id+"F28.imprint","IMPRINT",EDGE,{"disambiguationData":[TD([[subQ3,-1.0]])],"derivedFrom":subQ0}),1.0]])]});}
            var Q11;
            {var subQ0=sQuery(id+"F28.wireOp",EDGE,"E82");var subQ1=sQuery(id+"F0.wireOp",EDGE,"E0");var subQ2=makeQuery(id+"F2.opFillet","BLEND_EDGE",EDGE,{"blendedFrom":[makeQuery(id+"F1.opExtrude","CAP_EDGE",EDGE,{"disambiguationData":[OSD([subQ1])],"isStart":false}),makeQuery(id+"F1.opExtrude","CAP_FACE",FACE,{"disambiguationData":[OSD([subQ1,sQuery(id+"F0.wireOp",EDGE,"E1"),sQuery(id+"F0.wireOp",EDGE,"E2"),sQuery(id+"F0.wireOp",EDGE,"E3"),sQuery(id+"F0.wireOp",EDGE,"E4")])],"isStart":false})],"blendedInto":[makeQuery(id+"F1.opExtrude","CAP_FACE",FACE,{"disambiguationData":[OSD([subQ1,sQuery(id+"F0.wireOp",EDGE,"E1"),sQuery(id+"F0.wireOp",EDGE,"E2"),sQuery(id+"F0.wireOp",EDGE,"E3"),sQuery(id+"F0.wireOp",EDGE,"E4")])],"isStart":false})]});var subQ3=makeQuery(id+"F28.imprint","INTERSECT",VERTEX,{"disambiguationData":[OD(0.0)],"derivedFrom":[subQ2,subQ0]});Q11=makeQuery(id+"F28.imprint","IMPRINT",FACE,{"disambiguationData":[TD([[makeQuery(id+"F28.imprint","IMPRINT",EDGE,{"disambiguationData":[TD([[subQ3,1.0]])],"derivedFrom":subQ0}),1.0]])]});}
            extrude(context, id + "F29", {"entities" : qUnion([Q0, Q1, Q2, Q3, Q4, Q5, Q6, Q7, Q8, Q9, Q10, Q11]), "operationType" : NewBodyOperationType.ADD, "depth" : 3 * mm, "offsetDistance" : 25 * mm});
        }
        {
            var Q0;
            Q0=makeQuery(id+"F19.boolean.opBoolean","COPY",FACE,{"derivedFrom":makeQuery(id+"F19.opExtrude","SWEPT_FACE",FACE,{"disambiguationData":[OSD([sQuery(id+"F18.wireOp",EDGE,"E56.MirrorCS"),sQuery(id+"F18.wireOp",EDGE,"E58.MirrorCS")])]})});
            var sketch = newSketch(context, id + "F30", { "sketchPlane" : qUnion([Q0])});
            skLineSegment(sketch, "E87.bottom", {"start": v(18.83, -8.9) * mm, "end": v(23.86, -8.9) * mm});
            skLineSegment(sketch, "E87.top", {"start": v(18.83, -14.47) * mm, "end": v(23.86, -14.47) * mm});
            skLineSegment(sketch, "E87.left", {"start": v(18.83, -8.9) * mm, "end": v(18.83, -14.47) * mm});
            skLineSegment(sketch, "E87.right", {"start": v(23.86, -8.9) * mm, "end": v(23.86, -14.47) * mm});
            skSolve(sketch);
        }
        {
            var Q0;
            {var subQ0=sQuery(id+"F30.wireOp",EDGE,"E87.bottom");Q0=makeQuery(id+"F30.imprint","IMPRINT",FACE,{"disambiguationData":[TD([[makeQuery(id+"F30.imprint","IMPRINT",EDGE,{"derivedFrom":subQ0}),-1.0]])]});}
            extrude(context, id + "F31", {"entities" : qUnion([Q0]), "operationType" : NewBodyOperationType.ADD, "depth" : 2 * mm, "offsetDistance" : 25 * mm});
        }
        {
            var Q0;
            Q0=makeQuery(id+"F31.opExtrude","SWEPT_FACE",FACE,{"disambiguationData":[OSD([sQuery(id+"F30.wireOp",EDGE,"E87.right")])]});
            var sketch = newSketch(context, id + "F32", { "sketchPlane" : qUnion([Q0])});
            skCircle(sketch, "E88", {"center": v(-60, -11.07) * mm, "radius": 1.35 * mm});
            skCircle(sketch, "E89", {"center": v(-54, -11.07) * mm, "radius": 1.35 * mm});
            skCircle(sketch, "E90", {"center": v(-66, -11.07) * mm, "radius": 2 * mm});
            skCircle(sketch, "E91.MirrorC", {"center": v(54, -11.07) * mm, "radius": 1.35 * mm});
            skCircle(sketch, "E92.MirrorC", {"center": v(60, -11.07) * mm, "radius": 1.35 * mm});
            skCircle(sketch, "E93.MirrorC", {"center": v(66, -11.07) * mm, "radius": 2 * mm});
            skSolve(sketch);
        }
        {
            var Q0;
            Q0=makeQuery(id+"F32.imprint","IMPRINT",FACE,{"disambiguationData":[TD([[makeQuery(id+"F32.imprint","IMPRINT",EDGE,{"derivedFrom":sQuery(id+"F32.wireOp",EDGE,"E90")}),1.0]])]});
            var Q1;
            Q1=makeQuery(id+"F32.imprint","IMPRINT",FACE,{"disambiguationData":[TD([[makeQuery(id+"F32.imprint","IMPRINT",EDGE,{"derivedFrom":sQuery(id+"F32.wireOp",EDGE,"E88")}),1.0]])]});
            var Q2;
            Q2=makeQuery(id+"F32.imprint","IMPRINT",FACE,{"disambiguationData":[TD([[makeQuery(id+"F32.imprint","IMPRINT",EDGE,{"derivedFrom":sQuery(id+"F32.wireOp",EDGE,"E89")}),1.0]])]});
            extrude(context, id + "F33", {"entities" : qUnion([Q0, Q1, Q2]), "operationType" : NewBodyOperationType.ADD, "depth" : 7 * mm, "offsetDistance" : 25 * mm});
        }
        {
            var Q0;
            Q0=makeQuery(id+"F31.opExtrude","CAP_FACE",FACE,{"disambiguationData":[OSD([sQuery(id+"F15.wireOp",EDGE,"E37"),sQuery(id+"F18.wireOp",EDGE,"E56.MirrorCS"),sQuery(id+"F18.wireOp",EDGE,"E58.MirrorCS"),sQuery(id+"F30.wireOp",EDGE,"E87.bottom"),sQuery(id+"F30.wireOp",EDGE,"E87.left"),sQuery(id+"F30.wireOp",EDGE,"E87.right")])],"isStart":false});
            extrude(context, id + "F34", {"entities" : qUnion([Q0]), "operationType" : NewBodyOperationType.REMOVE, "oppositeDirection" : true, "depth" : 2 * mm, "offsetDistance" : 25 * mm});
        }
        {
            var Q0;
            Q0=makeQuery(id+"F15.imprint","IMPRINT",FACE,{"disambiguationData":[TD([[makeQuery(id+"F15.imprint","IMPRINT",EDGE,{"derivedFrom":sQuery(id+"F15.wireOp",EDGE,"E38")}),1.0]])]});
            extrude(context, id + "F35", {"entities" : qUnion([Q0]), "operationType" : NewBodyOperationType.ADD, "oppositeDirection" : true, "depth" : 27.5 * mm, "offsetDistance" : 25 * mm});
        }
        {
            var Q0;
            {var subQ0=sQuery(id+"F15.wireOp",EDGE,"E37");var subQ5=sQuery(id+"F0.wireOp",EDGE,"E1");Q0=makeQuery(id+"F31.boolean.opBoolean","MERGE",FACE,{"derivedFrom":[makeQuery(id+"Fm2CwqMFOKmotD7_1.boolean.opBoolean","MERGE",FACE,{"derivedFrom":[makeQuery(id+"F16.boolean.opBoolean","SPLIT",FACE,{"disambiguationData":[TD([makeQuery(id+"F2.opFillet","BLEND_FACE",FACE,{"disambiguationData":[OSD([subQ5]),TDD([makeQuery(id+"F1.opExtrude","CAP_EDGE",EDGE,{"disambiguationData":[OSD([subQ5])],"isStart":true})])]})])],"derivedFrom":makeQuery(id+"F16.opExtrude","SWEPT_FACE",FACE,{"disambiguationData":[OSD([subQ0])]})}),makeQuery(id+"Fm2CwqMFOKmotD7_1.opExtrude","SWEPT_FACE",FACE,{"disambiguationData":[OSD([subQ0])]})]}),makeQuery(id+"F31.opExtrude","SWEPT_FACE",FACE,{"disambiguationData":[OSD([subQ0,sQuery(id+"F18.wireOp",EDGE,"E56.MirrorCS"),sQuery(id+"F18.wireOp",EDGE,"E58.MirrorCS")])]})]});}
            var sketch = newSketch(context, id + "F36", { "sketchPlane" : qUnion([Q0])});
            skCircle(sketch, "E94", {"center": v(-53.98, 6.22) * mm, "radius": 9.5 * mm});
            skLineSegment(sketch, "E95", {"start": v(-53.98, 6.22) * mm, "end": v(-53.98, 9.22) * mm});
            skLineSegment(sketch, "E96", {"start": v(-53.98, 9.22) * mm, "end": v(-20.65, 14.22) * mm});
            skLineSegment(sketch, "E97", {"start": v(-20.65, 14.22) * mm, "end": v(-20.65, 8.22) * mm});
            skLineSegment(sketch, "E98", {"start": v(-20.65, 8.22) * mm, "end": v(-53.98, 6.22) * mm});
            skLineSegment(sketch, "E99", {"start": v(-53.98, 6.22) * mm, "end": v(-53.98, 3.22) * mm});
            skLineSegment(sketch, "E100", {"start": v(-53.98, 3.22) * mm, "end": v(-20.65, 3.22) * mm});
            skLineSegment(sketch, "E101", {"start": v(-20.65, 3.22) * mm, "end": v(-20.65, 8.22) * mm});
            skLineSegment(sketch, "E102.bottom", {"start": v(-77.85, 20.22) * mm, "end": v(-97.85, 20.22) * mm});
            skLineSegment(sketch, "E102.top", {"start": v(-77.85, 14.22) * mm, "end": v(-97.85, 14.22) * mm});
            skLineSegment(sketch, "E102.left", {"start": v(-77.85, 20.22) * mm, "end": v(-77.85, 14.22) * mm});
            skLineSegment(sketch, "E102.right", {"start": v(-97.85, 20.22) * mm, "end": v(-97.85, 14.22) * mm});
            skLineSegment(sketch, "E103.MirrorCS", {"start": v(53.98, 3.22) * mm, "end": v(20.65, 3.22) * mm});
            skLineSegment(sketch, "E104.MirrorCS", {"start": v(20.65, 8.22) * mm, "end": v(53.98, 6.22) * mm});
            skLineSegment(sketch, "E105.MirrorCS", {"start": v(53.98, 6.22) * mm, "end": v(53.98, 3.22) * mm});
            skLineSegment(sketch, "E106.MirrorCS", {"start": v(53.98, 6.22) * mm, "end": v(53.98, 9.22) * mm});
            skLineSegment(sketch, "E107.MirrorCS", {"start": v(53.98, 9.22) * mm, "end": v(20.65, 14.22) * mm});
            skCircle(sketch, "E108.MirrorC", {"center": v(53.98, 6.22) * mm, "radius": 9.5 * mm});
            skLineSegment(sketch, "E109.MirrorCS", {"start": v(20.65, 3.22) * mm, "end": v(20.65, 8.22) * mm});
            skLineSegment(sketch, "E110.MirrorCS", {"start": v(20.65, 14.22) * mm, "end": v(20.65, 8.22) * mm});
            skLineSegment(sketch, "E111.MirrorCS", {"start": v(77.85, 14.22) * mm, "end": v(97.85, 14.22) * mm});
            skLineSegment(sketch, "E112.MirrorCS", {"start": v(97.85, 20.22) * mm, "end": v(97.85, 14.22) * mm});
            skLineSegment(sketch, "E113.MirrorCS", {"start": v(77.85, 20.22) * mm, "end": v(77.85, 14.22) * mm});
            skLineSegment(sketch, "E114.MirrorCS", {"start": v(77.85, 20.22) * mm, "end": v(97.85, 20.22) * mm});
            skSolve(sketch);
        }
        {
            var Q0;
            Q0=makeQuery(id+"F36.imprint","IMPRINT",FACE,{"disambiguationData":[TD([[makeQuery(id+"F36.imprint","IMPRINT",EDGE,{"derivedFrom":sQuery(id+"F36.wireOp",EDGE,"E102.bottom")}),1.0]])]});
            extrude(context, id + "F37", {"entities" : qUnion([Q0]), "operationType" : NewBodyOperationType.ADD, "depth" : 2 * mm, "offsetDistance" : 25 * mm});
        }
        {
            var Q0;
            Q0=makeQuery(id+"F37.opExtrude","SWEPT_FACE",FACE,{"disambiguationData":[OSD([sQuery(id+"F36.wireOp",EDGE,"E102.bottom")])]});
            var sketch = newSketch(context, id + "F38", { "sketchPlane" : qUnion([Q0])});
            skCircle(sketch, "E115", {"center": v(-94.35, -18.87) * mm, "radius": 3.21 * mm});
            skCircle(sketch, "E116", {"center": v(-87.85, -18.87) * mm, "radius": 3.21 * mm});
            skCircle(sketch, "E117", {"center": v(-81.35, -18.87) * mm, "radius": 3.21 * mm});
            skCircle(sketch, "E118.MirrorC", {"center": v(81.35, -18.87) * mm, "radius": 3.21 * mm});
            skCircle(sketch, "E119.MirrorC", {"center": v(87.85, -18.87) * mm, "radius": 3.21 * mm});
            skCircle(sketch, "E120.MirrorC", {"center": v(94.35, -18.87) * mm, "radius": 3.21 * mm});
            skSolve(sketch);
        }
        {
            var Q0;
            {var subQ0=sQuery(id+"F38.wireOp",EDGE,"E115");var subQ1=makeQuery(id+"F37.opExtrude","CAP_EDGE",EDGE,{"disambiguationData":[OSD([sQuery(id+"F36.wireOp",EDGE,"E102.bottom")])],"isStart":false});var subQ2=makeQuery(id+"F38.imprint","INTERSECT",VERTEX,{"disambiguationData":[OD(0.0)],"derivedFrom":[subQ1,subQ0]});Q0=makeQuery(id+"F38.imprint","IMPRINT",FACE,{"disambiguationData":[TD([[makeQuery(id+"F38.imprint","IMPRINT",EDGE,{"disambiguationData":[TD([[subQ2,-1.0]])],"derivedFrom":subQ0}),1.0]])]});}
            var Q1;
            {var subQ0=sQuery(id+"F38.wireOp",EDGE,"E116");var subQ1=makeQuery(id+"F37.opExtrude","CAP_EDGE",EDGE,{"disambiguationData":[OSD([sQuery(id+"F36.wireOp",EDGE,"E102.bottom")])],"isStart":false});var subQ2=makeQuery(id+"F38.imprint","INTERSECT",VERTEX,{"disambiguationData":[OD(0.0)],"derivedFrom":[subQ1,subQ0]});Q1=makeQuery(id+"F38.imprint","IMPRINT",FACE,{"disambiguationData":[TD([[makeQuery(id+"F38.imprint","IMPRINT",EDGE,{"disambiguationData":[TD([[subQ2,-1.0]])],"derivedFrom":subQ0}),1.0]])]});}
            var Q2;
            {var subQ0=sQuery(id+"F38.wireOp",EDGE,"E117");var subQ1=makeQuery(id+"F37.opExtrude","CAP_EDGE",EDGE,{"disambiguationData":[OSD([sQuery(id+"F36.wireOp",EDGE,"E102.bottom")])],"isStart":false});var subQ2=makeQuery(id+"F38.imprint","INTERSECT",VERTEX,{"disambiguationData":[OD(0.0)],"derivedFrom":[subQ1,subQ0]});Q2=makeQuery(id+"F38.imprint","IMPRINT",FACE,{"disambiguationData":[TD([[makeQuery(id+"F38.imprint","IMPRINT",EDGE,{"disambiguationData":[TD([[subQ2,1.0]])],"derivedFrom":subQ0}),1.0]])]});}
            var Q3;
            {var subQ0=sQuery(id+"F38.wireOp",EDGE,"E115");var subQ1=makeQuery(id+"F37.opExtrude","CAP_EDGE",EDGE,{"disambiguationData":[OSD([sQuery(id+"F36.wireOp",EDGE,"E102.bottom")])],"isStart":false});var subQ2=makeQuery(id+"F38.imprint","INTERSECT",VERTEX,{"disambiguationData":[OD(0.0)],"derivedFrom":[subQ1,subQ0]});Q3=makeQuery(id+"F38.imprint","IMPRINT",FACE,{"disambiguationData":[TD([[makeQuery(id+"F38.imprint","IMPRINT",EDGE,{"disambiguationData":[TD([[subQ2,1.0]])],"derivedFrom":subQ0}),1.0]])]});}
            var Q4;
            {var subQ0=sQuery(id+"F38.wireOp",EDGE,"E116");var subQ1=makeQuery(id+"F37.opExtrude","CAP_EDGE",EDGE,{"disambiguationData":[OSD([sQuery(id+"F36.wireOp",EDGE,"E102.bottom")])],"isStart":false});var subQ2=makeQuery(id+"F38.imprint","INTERSECT",VERTEX,{"disambiguationData":[OD(0.0)],"derivedFrom":[subQ1,subQ0]});Q4=makeQuery(id+"F38.imprint","IMPRINT",FACE,{"disambiguationData":[TD([[makeQuery(id+"F38.imprint","IMPRINT",EDGE,{"disambiguationData":[TD([[subQ2,1.0]])],"derivedFrom":subQ0}),1.0]])]});}
            var Q5;
            {var subQ0=sQuery(id+"F38.wireOp",EDGE,"E117");var subQ1=makeQuery(id+"F37.opExtrude","CAP_EDGE",EDGE,{"disambiguationData":[OSD([sQuery(id+"F36.wireOp",EDGE,"E102.bottom")])],"isStart":false});var subQ2=makeQuery(id+"F38.imprint","INTERSECT",VERTEX,{"disambiguationData":[OD(0.0)],"derivedFrom":[subQ1,subQ0]});Q5=makeQuery(id+"F38.imprint","IMPRINT",FACE,{"disambiguationData":[TD([[makeQuery(id+"F38.imprint","IMPRINT",EDGE,{"disambiguationData":[TD([[subQ2,-1.0]])],"derivedFrom":subQ0}),1.0]])]});}
            extrude(context, id + "F39", {"entities" : qUnion([Q0, Q1, Q2, Q3, Q4, Q5]), "operationType" : NewBodyOperationType.ADD, "oppositeDirection" : true, "depth" : 20 * mm, "offsetDistance" : 25 * mm, "hasSecondDirection" : true, "secondDirectionOppositeDirection" : false, "secondDirectionDepth" : 5 * mm});
        }
        {
            var Q0;
            Q0=makeQuery(id+"F39.opExtrude","CAP_EDGE",EDGE,{"disambiguationData":[OSD([sQuery(id+"F38.wireOp",EDGE,"E115")])],"isStart":true});
            var Q1;
            Q1=makeQuery(id+"F39.opExtrude","CAP_EDGE",EDGE,{"disambiguationData":[OSD([sQuery(id+"F38.wireOp",EDGE,"E116")])],"isStart":true});
            var Q2;
            Q2=makeQuery(id+"F39.opExtrude","CAP_EDGE",EDGE,{"disambiguationData":[OSD([sQuery(id+"F38.wireOp",EDGE,"E117")])],"isStart":true});
            var Q3;
            Q3=makeQuery(id+"F39.opExtrude","CAP_EDGE",EDGE,{"disambiguationData":[OSD([sQuery(id+"F38.wireOp",EDGE,"E118.MirrorC")])],"isStart":true});
            var Q4;
            Q4=makeQuery(id+"F39.opExtrude","CAP_EDGE",EDGE,{"disambiguationData":[OSD([sQuery(id+"F38.wireOp",EDGE,"E119.MirrorC")])],"isStart":true});
            var Q5;
            Q5=makeQuery(id+"F39.opExtrude","CAP_EDGE",EDGE,{"disambiguationData":[OSD([sQuery(id+"F38.wireOp",EDGE,"E120.MirrorC")])],"isStart":true});
            fillet(context, id + "F40", {"entities" : qUnion([Q0, Q1, Q2, Q3, Q4, Q5]), "radius" : 3 * mm, "tangentPropagation" : true, "allowEdgeOverflow" : false});
        }
        {
            var Q0;
            Q0=makeQuery(id+"F21.opExtrude","CAP_EDGE",EDGE,{"disambiguationData":[OSD([sQuery(id+"F20.wireOp",EDGE,"E59")])],"isStart":false});
            fillet(context, id + "F41", {"entities" : qUnion([Q0]), "radius" : 1.99 * mm, "tangentPropagation" : true, "defaultsChanged" : true, "vertexSettings" : [], "allowEdgeOverflow" : false});
        }
        {
            var Q0;
            Q0=makeQuery(id+"F7.opExtrude","SWEPT_EDGE",EDGE,{"disambiguationData":[OSD([sQuery(id+"F6.wireOp",EDGE,"E24"),sQuery(id+"F6.wireOp",EDGE,"E25")])]});
            fillet(context, id + "F42", {"entities" : qUnion([Q0]), "radius" : 5 * mm, "tangentPropagation" : true, "allowEdgeOverflow" : false});
        }
        {
            var Q0;
            {var subQ2=sQuery(id+"F36.wireOp",EDGE,"E95");Q0=makeQuery(id+"F36.imprint","IMPRINT",FACE,{"disambiguationData":[TD([[makeQuery(id+"F36.imprint","IMPRINT",EDGE,{"derivedFrom":subQ2}),1.0]])]});}
            var Q1;
            {var subQ5=sQuery(id+"F36.wireOp",EDGE,"E95");Q1=makeQuery(id+"F36.imprint","IMPRINT",FACE,{"disambiguationData":[TD([[makeQuery(id+"F36.imprint","IMPRINT",EDGE,{"derivedFrom":subQ5}),-1.0]])]});}
            var Q2;
            {var subQ5=sQuery(id+"F36.wireOp",EDGE,"E99");Q2=makeQuery(id+"F36.imprint","IMPRINT",FACE,{"disambiguationData":[TD([[makeQuery(id+"F36.imprint","IMPRINT",EDGE,{"derivedFrom":subQ5}),1.0]])]});}
            extrude(context, id + "F43", {"entities" : qUnion([Q0, Q1, Q2]), "operationType" : NewBodyOperationType.ADD, "depth" : 2 * mm, "offsetDistance" : 25 * mm});
        }
        {
            var Q0;
            Q0=makeQuery(id+"F1.opExtrude","SWEPT_BODY",BODY,{"disambiguationData":[OSD([sQuery(id+"F0.wireOp",EDGE,"E0"),sQuery(id+"F0.wireOp",EDGE,"E1"),sQuery(id+"F0.wireOp",EDGE,"E2"),sQuery(id+"F0.wireOp",EDGE,"E3"),sQuery(id+"F0.wireOp",EDGE,"E4")])]});
            var Q1;
            Q1=qCreatedBy(makeId("Right.planeOp"),FACE);
            mirror(context, id + "F44", {"entities" : qUnion([Q0]), "mirrorPlane" : qUnion([Q1])});
        }
        {
            var Q0;
            {var subQ0=sQuery(id+"F15.wireOp",EDGE,"E37");Q0=makeQuery(id+"F44.opPattern","COPY",FACE,{"derivedFrom":makeQuery(id+"F31.boolean.opBoolean","MERGE",FACE,{"derivedFrom":[makeQuery(id+"F17.boolean.opBoolean","MERGE",FACE,{"derivedFrom":[makeQuery(id+"F16.opExtrude","SWEPT_FACE",FACE,{"disambiguationData":[OSD([subQ0])]}),makeQuery(id+"F17.opExtrude","SWEPT_FACE",FACE,{"disambiguationData":[OSD([subQ0])]})]}),makeQuery(id+"F31.opExtrude","SWEPT_FACE",FACE,{"disambiguationData":[OSD([subQ0,sQuery(id+"F18.wireOp",EDGE,"E56.MirrorCS"),sQuery(id+"F18.wireOp",EDGE,"E58.MirrorCS")])]})]}),"instanceName":"1"});}
            var sketch = newSketch(context, id + "F45", { "sketchPlane" : qUnion([Q0])});
            skLineSegment(sketch, "E121.bottom", {"start": v(19.85, 12.22) * mm, "end": v(23.85, 12.22) * mm});
            skLineSegment(sketch, "E121.top", {"start": v(19.85, -2.78) * mm, "end": v(23.85, -2.78) * mm});
            skLineSegment(sketch, "E121.left", {"start": v(19.85, 12.22) * mm, "end": v(19.85, -2.78) * mm});
            skLineSegment(sketch, "E121.right", {"start": v(23.85, 12.22) * mm, "end": v(23.85, -2.78) * mm});
            skLineSegment(sketch, "E122.MirrorCS", {"start": v(-19.85, 12.22) * mm, "end": v(-19.85, -2.78) * mm});
            skLineSegment(sketch, "E123.MirrorCS", {"start": v(-19.85, 12.22) * mm, "end": v(-23.85, 12.22) * mm});
            skLineSegment(sketch, "E124.MirrorCS", {"start": v(-19.85, -2.78) * mm, "end": v(-23.85, -2.78) * mm});
            skLineSegment(sketch, "E125.MirrorCS", {"start": v(-23.85, 12.22) * mm, "end": v(-23.85, -2.78) * mm});
            skCircle(sketch, "E126", {"center": v(-53.98, 6.22) * mm, "radius": 9.5 * mm});
            skCircle(sketch, "E127.MirrorC", {"center": v(53.98, 6.22) * mm, "radius": 9.5 * mm});
            skLineSegment(sketch, "E128", {"start": v(-53.98, 6.22) * mm, "end": v(-53.98, 10.22) * mm});
            skLineSegment(sketch, "E129", {"start": v(-53.98, 10.22) * mm, "end": v(-23.85, 12.22) * mm});
            skLineSegment(sketch, "E130", {"start": v(-53.98, 6.22) * mm, "end": v(-53.98, 2.22) * mm});
            skLineSegment(sketch, "E131", {"start": v(-53.98, 2.22) * mm, "end": v(-23.85, -2.78) * mm});
            skLineSegment(sketch, "E132.MirrorCS", {"start": v(53.98, 10.22) * mm, "end": v(23.85, 12.22) * mm});
            skLineSegment(sketch, "E133.MirrorCS", {"start": v(53.98, 2.22) * mm, "end": v(23.85, -2.78) * mm});
            skLineSegment(sketch, "E134.MirrorCS", {"start": v(53.98, 6.22) * mm, "end": v(53.98, 2.22) * mm});
            skLineSegment(sketch, "E135.MirrorCS", {"start": v(53.98, 6.22) * mm, "end": v(53.98, 10.22) * mm});
            skSolve(sketch);
        }
        {
            var Q0;
            Q0=makeQuery(id+"F45.imprint","IMPRINT",FACE,{"disambiguationData":[TD([[makeQuery(id+"F45.imprint","IMPRINT",EDGE,{"derivedFrom":sQuery(id+"F45.wireOp",EDGE,"E121.bottom")}),-1.0]])]});
            extrude(context, id + "F46", {"entities" : qUnion([Q0]), "depth" : 19 * mm, "offsetDistance" : 25 * mm});
        }
        {
            var Q0;
            Q0=makeQuery(id+"F46.opExtrude","SWEPT_FACE",FACE,{"disambiguationData":[OSD([sQuery(id+"F45.wireOp",EDGE,"E121.right")])]});
            var sketch = newSketch(context, id + "F47", { "sketchPlane" : qUnion([Q0])});
            skCircle(sketch, "E136", {"center": v(-7.4, -33.06) * mm, "radius": 9.5 * mm});
            skLineSegment(sketch, "E137", {"start": v(-7.4, -33.06) * mm, "end": v(-3.4, -32.96) * mm});
            skLineSegment(sketch, "E138", {"start": v(-3.4, -32.96) * mm, "end": v(3.19, -16.1) * mm});
            skLineSegment(sketch, "E139", {"start": v(-7.4, -33.06) * mm, "end": v(-11.4, -33.16) * mm});
            skLineSegment(sketch, "E140", {"start": v(-11.4, -33.16) * mm, "end": v(-11.82, -16.21) * mm});
            skLineSegment(sketch, "E141", {"start": v(-11.82, -16.21) * mm, "end": v(3.19, -16.1) * mm});
            skLineSegment(sketch, "E142", {"start": v(-3.4, -32.96) * mm, "end": v(3.6, -32.79) * mm});
            skLineSegment(sketch, "E143", {"start": v(3.6, -32.79) * mm, "end": v(3.19, -16.1) * mm});
            skLineSegment(sketch, "E144", {"start": v(82.39, -11.86) * mm, "end": v(89.01, -15.2) * mm});
            skLineSegment(sketch, "E145", {"start": v(94.1, -14.87) * mm, "end": v(98.22, -12.05) * mm});
            skLineSegment(sketch, "E146", {"start": v(98.22, -12.05) * mm, "end": v(92.28, -9.7) * mm});
            skLineSegment(sketch, "E147", {"start": v(92.28, -9.7) * mm, "end": v(82.39, -11.86) * mm});
            skCircle(sketch, "E148", {"center": v(91.66, -14.68) * mm, "radius": 4 * mm});
            skPoint(sketch, "E149.visualSharp", {"position": v(91.66, -16.54) * mm});
            skArc(sketch, "E149.filletArc", {"start": v(89.01, -15.2) * mm, "mid": v(91.6, -15.74) * mm, "end": v(94.1, -14.87) * mm});
            skPoint(sketch, "E150.visualSharp", {"position": v(98.22, -12.05) * mm});
            skSolve(sketch);
        }
        {
            var Q0;
            {var subQ5=sQuery(id+"F47.wireOp",EDGE,"E143");Q0=makeQuery(id+"F47.imprint","IMPRINT",FACE,{"disambiguationData":[TD([[makeQuery(id+"F47.imprint","IMPRINT",EDGE,{"derivedFrom":subQ5}),1.0]])]});}
            extrude(context, id + "F48", {"entities" : qUnion([Q0]), "operationType" : NewBodyOperationType.REMOVE, "oppositeDirection" : true, "depth" : 4 * mm, "offsetDistance" : 25 * mm});
        }
        {
            var Q0;
            {var subQ1=sQuery(id+"F47.wireOp",EDGE,"E137");Q0=makeQuery(id+"F47.imprint","IMPRINT",FACE,{"disambiguationData":[TD([[makeQuery(id+"F47.imprint","IMPRINT",EDGE,{"derivedFrom":subQ1}),-1.0]])]});}
            var Q1;
            {var subQ1=sQuery(id+"F47.wireOp",EDGE,"E137");Q1=makeQuery(id+"F47.imprint","IMPRINT",FACE,{"disambiguationData":[TD([[makeQuery(id+"F47.imprint","IMPRINT",EDGE,{"derivedFrom":subQ1}),1.0]])]});}
            extrude(context, id + "F49", {"entities" : qUnion([Q0, Q1]), "operationType" : NewBodyOperationType.ADD, "oppositeDirection" : true, "depth" : 4 * mm, "offsetDistance" : 25 * mm});
        }
        {
            var Q0;
            {var subQ0=sQuery(id+"F47.wireOp",EDGE,"E146");Q0=makeQuery(id+"F47.imprint","IMPRINT",FACE,{"disambiguationData":[TD([[makeQuery(id+"F47.imprint","IMPRINT",EDGE,{"derivedFrom":subQ0}),1.0]])]});}
            var Q1;
            {var subQ0=sQuery(id+"F47.wireOp",EDGE,"E149.filletArc");Q1=makeQuery(id+"F47.imprint","IMPRINT",FACE,{"disambiguationData":[TD([[makeQuery(id+"F47.imprint","IMPRINT",EDGE,{"derivedFrom":subQ0}),1.0]])]});}
            var Q2;
            {var subQ0=sQuery(id+"F47.wireOp",EDGE,"E149.filletArc");Q2=makeQuery(id+"F47.imprint","IMPRINT",FACE,{"disambiguationData":[TD([[makeQuery(id+"F47.imprint","IMPRINT",EDGE,{"derivedFrom":subQ0}),-1.0]])]});}
            extrude(context, id + "F50", {"entities" : qUnion([Q0, Q1, Q2]), "operationType" : NewBodyOperationType.ADD, "oppositeDirection" : true, "depth" : 24 * mm, "offsetDistance" : 25 * mm});
        }
        {
            var Q0;
            Q0=makeQuery(id+"F50.opExtrude","CAP_FACE",FACE,{"disambiguationData":[OSD([sQuery(id+"F47.wireOp",EDGE,"E144"),sQuery(id+"F47.wireOp",EDGE,"E145"),sQuery(id+"F47.wireOp",EDGE,"E146"),sQuery(id+"F47.wireOp",EDGE,"E147"),sQuery(id+"F47.wireOp",EDGE,"E148")])],"isStart":true});
            extrude(context, id + "F51", {"entities" : qUnion([Q0]), "operationType" : NewBodyOperationType.REMOVE, "oppositeDirection" : true, "depth" : 22.5 * mm, "offsetDistance" : 25 * mm});
        }
        {
            var Q0;
            {var subQ5=sQuery(id+"F47.wireOp",EDGE,"E143");Q0=makeQuery(id+"F47.imprint","IMPRINT",FACE,{"disambiguationData":[TD([[makeQuery(id+"F47.imprint","IMPRINT",EDGE,{"derivedFrom":subQ5}),1.0]])]});}
            extrude(context, id + "F52", {"entities" : qUnion([Q0]), "operationType" : NewBodyOperationType.REMOVE, "oppositeDirection" : true, "depth" : 245 * mm, "offsetDistance" : 25 * mm});
        }
        {
            var Q0;
            Q0=makeQuery(id+"F50.opExtrude","CAP_FACE",FACE,{"disambiguationData":[OSD([sQuery(id+"F47.wireOp",EDGE,"E144"),sQuery(id+"F47.wireOp",EDGE,"E145"),sQuery(id+"F47.wireOp",EDGE,"E146"),sQuery(id+"F47.wireOp",EDGE,"E147"),sQuery(id+"F47.wireOp",EDGE,"E148")])],"isStart":false});
            extrude(context, id + "F53", {"entities" : qUnion([Q0]), "operationType" : NewBodyOperationType.ADD, "depth" : 1.5 * mm, "offsetDistance" : 25 * mm});
        }
        {
            var Q0;
            Q0=makeQuery(id+"F46.opExtrude","SWEPT_BODY",BODY,{"disambiguationData":[OSD([sQuery(id+"F45.wireOp",EDGE,"E121.bottom"),sQuery(id+"F45.wireOp",EDGE,"E121.top"),sQuery(id+"F45.wireOp",EDGE,"E121.left"),sQuery(id+"F45.wireOp",EDGE,"E121.right")])]});
            var Q1;
            Q1=qCreatedBy(makeId("Right.planeOp"),FACE);
            mirror(context, id + "F54", {"entities" : qUnion([Q0]), "mirrorPlane" : qUnion([Q1])});
        }
        {
            var Q0;
            {var subQ2=sQuery(id+"F0.wireOp",EDGE,"E9");Q0=makeQuery(id+"F0.imprint","IMPRINT",FACE,{"disambiguationData":[TD([[makeQuery(id+"F0.imprint","IMPRINT",EDGE,{"derivedFrom":subQ2}),1.0]])]});}
            extrude(context, id + "F55", {"entities" : qUnion([Q0]), "operationType" : NewBodyOperationType.ADD, "depth" : 25 * mm, "offsetDistance" : 25 * mm, "symmetric" : true});
        }
        {
            var Q0;
            Q0=makeQuery(id+"F55.opExtrude","CAP_EDGE",EDGE,{"disambiguationData":[OSD([sQuery(id+"F0.wireOp",EDGE,"E10")])],"isStart":false});
            var Q1;
            Q1=makeQuery(id+"F55.opExtrude","CAP_EDGE",EDGE,{"disambiguationData":[OSD([sQuery(id+"F0.wireOp",EDGE,"E10")])],"isStart":true});
            var Q2;
            Q2=makeQuery(id+"F55.opExtrude","SWEPT_EDGE",EDGE,{"disambiguationData":[OSD([sQuery(id+"F0.wireOp",EDGE,"E10"),sQuery(id+"F0.wireOp",EDGE,"E11")])]});
            fillet(context, id + "F56", {"entities" : qUnion([Q0, Q1, Q2]), "radius" : 5 * mm, "tangentPropagation" : true, "allowEdgeOverflow" : false});
        }
        {
            var Q0;
            Q0=makeQuery(id+"F11.boolean.opBoolean","COPY",EDGE,{"derivedFrom":makeQuery(id+"F11.opExtrude","CAP_EDGE",EDGE,{"disambiguationData":[OSD([sQuery(id+"F10.wireOp",EDGE,"E31")])],"isStart":false})});
            var Q1;
            Q1=makeQuery(id+"F11.boolean.opBoolean","COPY",EDGE,{"derivedFrom":makeQuery(id+"F11.opExtrude","CAP_EDGE",EDGE,{"disambiguationData":[OSD([sQuery(id+"F10.wireOp",EDGE,"E32")])],"isStart":false})});
            var Q2;
            Q2=makeQuery(id+"F16.boolean.opBoolean","INTERSECT",EDGE,{"derivedFrom":[makeQuery(id+"F11.boolean.opBoolean","COPY",FACE,{"derivedFrom":makeQuery(id+"F11.opExtrude","CAP_FACE",FACE,{"disambiguationData":[OSD([sQuery(id+"F10.wireOp",EDGE,"E27"),sQuery(id+"F10.wireOp",EDGE,"E28"),sQuery(id+"F10.wireOp",EDGE,"E29"),sQuery(id+"F10.wireOp",EDGE,"E30"),sQuery(id+"F10.wireOp",EDGE,"E31"),sQuery(id+"F10.wireOp",EDGE,"E32"),sQuery(id+"F10.wireOp",EDGE,"E33.bottom"),sQuery(id+"F10.wireOp",EDGE,"E33.top"),sQuery(id+"F10.wireOp",EDGE,"E33.right")])],"isStart":false})}),makeQuery(id+"F16.opExtrude","SWEPT_FACE",FACE,{"disambiguationData":[OSD([sQuery(id+"F15.wireOp",EDGE,"E36")])]})]});
            var Q3;
            Q3=makeQuery(id+"F11.boolean.opBoolean","COPY",EDGE,{"derivedFrom":makeQuery(id+"F11.opExtrude","CAP_EDGE",EDGE,{"disambiguationData":[OSD([sQuery(id+"F10.wireOp",EDGE,"E33.top")])],"isStart":false})});
            var Q4;
            Q4=makeQuery(id+"F16.boolean.opBoolean","INTERSECT",EDGE,{"derivedFrom":[makeQuery(id+"F11.boolean.opBoolean","COPY",FACE,{"derivedFrom":makeQuery(id+"F11.opExtrude","CAP_FACE",FACE,{"disambiguationData":[OSD([sQuery(id+"F10.wireOp",EDGE,"E27"),sQuery(id+"F10.wireOp",EDGE,"E28"),sQuery(id+"F10.wireOp",EDGE,"E29"),sQuery(id+"F10.wireOp",EDGE,"E30"),sQuery(id+"F10.wireOp",EDGE,"E31"),sQuery(id+"F10.wireOp",EDGE,"E32"),sQuery(id+"F10.wireOp",EDGE,"E33.bottom"),sQuery(id+"F10.wireOp",EDGE,"E33.top"),sQuery(id+"F10.wireOp",EDGE,"E33.right")])],"isStart":false})}),makeQuery(id+"F16.opExtrude","SWEPT_FACE",FACE,{"disambiguationData":[OSD([sQuery(id+"F15.wireOp",EDGE,"E35")])]})]});
            var Q5;
            Q5=makeQuery(id+"F11.boolean.opBoolean","COPY",EDGE,{"derivedFrom":makeQuery(id+"F11.opExtrude","CAP_EDGE",EDGE,{"disambiguationData":[OSD([sQuery(id+"F10.wireOp",EDGE,"E27")])],"isStart":false})});
            var Q6;
            Q6=makeQuery(id+"F11.boolean.opBoolean","COPY",EDGE,{"derivedFrom":makeQuery(id+"F11.opExtrude","CAP_EDGE",EDGE,{"disambiguationData":[OSD([sQuery(id+"F10.wireOp",EDGE,"E28")])],"isStart":false})});
            var Q7;
            Q7=makeQuery(id+"F11.boolean.opBoolean","COPY",EDGE,{"derivedFrom":makeQuery(id+"F11.opExtrude","CAP_EDGE",EDGE,{"disambiguationData":[OSD([sQuery(id+"F10.wireOp",EDGE,"E29"),sQuery(id+"F10.wireOp",EDGE,"E33.bottom")])],"isStart":false})});
            var Q8;
            Q8=makeQuery(id+"F11.boolean.opBoolean","COPY",EDGE,{"derivedFrom":makeQuery(id+"F11.opExtrude","CAP_EDGE",EDGE,{"disambiguationData":[OSD([sQuery(id+"F10.wireOp",EDGE,"E33.right")])],"isStart":false})});
            var Q9;
            Q9=makeQuery(id+"F11.boolean.opBoolean","COPY",EDGE,{"derivedFrom":makeQuery(id+"F11.opExtrude","SWEPT_EDGE",EDGE,{"disambiguationData":[OSD([sQuery(id+"F10.wireOp",EDGE,"E33.top"),sQuery(id+"F10.wireOp",EDGE,"E33.right")])]})});
            var Q10;
            Q10=makeQuery(id+"F16.boolean.opBoolean","INTERSECT",EDGE,{"derivedFrom":[makeQuery(id+"F11.boolean.opBoolean","COPY",FACE,{"derivedFrom":makeQuery(id+"F11.opExtrude","SWEPT_FACE",FACE,{"disambiguationData":[OSD([sQuery(id+"F10.wireOp",EDGE,"E33.top")])]})}),makeQuery(id+"F16.opExtrude","SWEPT_FACE",FACE,{"disambiguationData":[OSD([sQuery(id+"F15.wireOp",EDGE,"E36")])]})]});
            var Q11;
            {var subQ1=sQuery(id+"F15.wireOp",EDGE,"E35");var subQ2=sQuery(id+"F15.wireOp",EDGE,"E36");Q11=makeQuery(id+"F16.boolean.opBoolean","SPLIT",EDGE,{"disambiguationData":[TD([makeQuery(id+"F7.opExtrude","CAP_FACE",FACE,{"disambiguationData":[OSD([sQuery(id+"F6.wireOp",EDGE,"E24"),sQuery(id+"F6.wireOp",EDGE,"E25"),sQuery(id+"F6.wireOp",EDGE,"E26")])],"isStart":true})])],"derivedFrom":makeQuery(id+"F16.opExtrude","SWEPT_EDGE",EDGE,{"disambiguationData":[OSD([subQ1,subQ2])]})});}
            var Q12;
            Q12=makeQuery(id+"F16.boolean.opBoolean","INTERSECT",EDGE,{"derivedFrom":[makeQuery(id+"F11.boolean.opBoolean","COPY",FACE,{"derivedFrom":makeQuery(id+"F11.opExtrude","SWEPT_FACE",FACE,{"disambiguationData":[OSD([sQuery(id+"F10.wireOp",EDGE,"E31")])]})}),makeQuery(id+"F16.opExtrude","SWEPT_FACE",FACE,{"disambiguationData":[OSD([sQuery(id+"F15.wireOp",EDGE,"E35")])]})]});
            var Q13;
            Q13=makeQuery(id+"F11.boolean.opBoolean","COPY",EDGE,{"derivedFrom":makeQuery(id+"F11.opExtrude","SWEPT_EDGE",EDGE,{"disambiguationData":[OSD([sQuery(id+"F10.wireOp",EDGE,"E31"),sQuery(id+"F10.wireOp",EDGE,"E32")])]})});
            var Q14;
            Q14=makeQuery(id+"F11.boolean.opBoolean","COPY",EDGE,{"derivedFrom":makeQuery(id+"F11.opExtrude","SWEPT_EDGE",EDGE,{"disambiguationData":[OSD([sQuery(id+"F10.wireOp",EDGE,"E27"),sQuery(id+"F10.wireOp",EDGE,"E32")])]})});
            var Q15;
            Q15=makeQuery(id+"F11.boolean.opBoolean","COPY",EDGE,{"derivedFrom":makeQuery(id+"F11.opExtrude","SWEPT_EDGE",EDGE,{"disambiguationData":[OSD([sQuery(id+"F10.wireOp",EDGE,"E27"),sQuery(id+"F10.wireOp",EDGE,"E28")])]})});
            var Q16;
            Q16=makeQuery(id+"F11.boolean.opBoolean","COPY",EDGE,{"derivedFrom":makeQuery(id+"F11.opExtrude","SWEPT_EDGE",EDGE,{"disambiguationData":[OSD([sQuery(id+"F10.wireOp",EDGE,"E28"),sQuery(id+"F10.wireOp",EDGE,"E29")])]})});
            var Q17;
            Q17=makeQuery(id+"F11.boolean.opBoolean","COPY",EDGE,{"derivedFrom":makeQuery(id+"F11.opExtrude","SWEPT_EDGE",EDGE,{"disambiguationData":[OSD([sQuery(id+"F10.wireOp",EDGE,"E33.bottom"),sQuery(id+"F10.wireOp",EDGE,"E33.right")])]})});
            fillet(context, id + "F57", {"entities" : qUnion([Q0, Q1, Q2, Q3, Q4, Q5, Q6, Q7, Q8, Q9, Q10, Q11, Q12, Q13, Q14, Q15, Q16, Q17]), "radius" : 1 * mm, "tangentPropagation" : true, "allowEdgeOverflow" : false});
        }
    });
